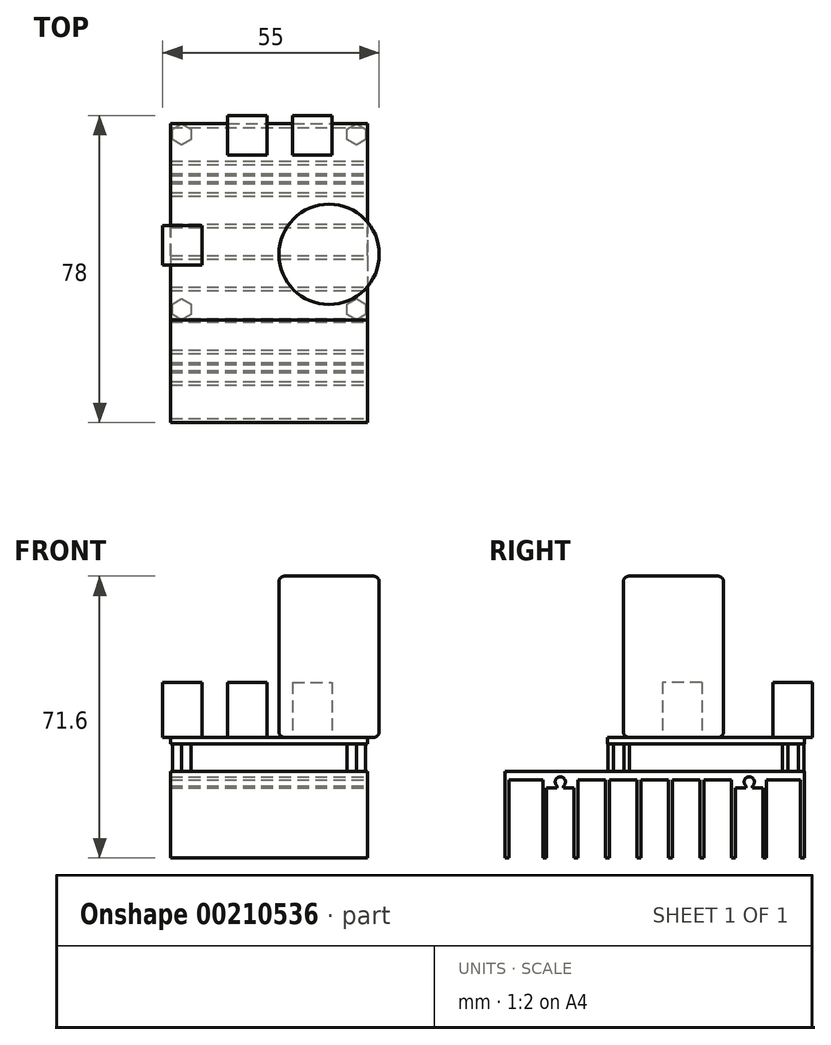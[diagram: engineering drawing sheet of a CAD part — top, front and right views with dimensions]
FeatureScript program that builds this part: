
annotation { "Feature Type Name" : "Feature", "Feature Type Description" : "" }
export const myFeature = defineFeature(function(context is Context, id is Id, definition is map)
    precondition{}
    {
        {
            var Q0;
            Q0=qCreatedBy(makeId("Top.planeOp"),FACE);
            var sketch = newSketch(context, id + "F0", { "sketchPlane" : qUnion([Q0])});
            skLineSegment(sketch, "E0.bottom", {"start": v(-25, 38) * mm, "end": v(25, 38) * mm});
            skLineSegment(sketch, "E0.top", {"start": v(-25, -38) * mm, "end": v(25, -38) * mm});
            skLineSegment(sketch, "E0.left", {"start": v(-25, 38) * mm, "end": v(-25, -38) * mm});
            skLineSegment(sketch, "E0.right", {"start": v(25, 38) * mm, "end": v(25, -38) * mm});
            skLineSegment(sketch, "E1", {"start": v(-25, 38) * mm, "end": v(25, -38) * mm, "construction": true});
            skSolve(sketch);
        }
        {
            var Q0;
            Q0=makeQuery(id+"F0.imprint","IMPRINT",FACE,{"disambiguationData":[TD([[makeQuery(id+"F0.imprint","IMPRINT",EDGE,{"derivedFrom":sQuery(id+"F0.wireOp",EDGE,"E0.bottom")}),-1.0]])]});
            extrude(context, id + "F1", {"entities" : qUnion([Q0]), "oppositeDirection" : true, "depth" : 22 * mm});
        }
        {
            var Q0;
            Q0=qCreatedBy(makeId("Right.planeOp"),FACE);
            var sketch = newSketch(context, id + "F2", { "sketchPlane" : qUnion([Q0])});
            skLineSegment(sketch, "E2.bottom", {"start": v(-37, -2.2) * mm, "end": v(-28.4, -2.2) * mm});
            skLineSegment(sketch, "E2.top", {"start": v(-37, -22) * mm, "end": v(-28.4, -22) * mm});
            skLineSegment(sketch, "E2.left", {"start": v(-37, -2.2) * mm, "end": v(-37, -22) * mm});
            skLineSegment(sketch, "E2.right", {"start": v(-28.4, -2.2) * mm, "end": v(-28.4, -22) * mm});
            skLineSegment(sketch, "E3", {"start": v(0, 0) * mm, "end": v(0, -2.2) * mm, "construction": true});
            skLineSegment(sketch, "E4.bottom", {"start": v(-3.5, -22) * mm, "end": v(3.5, -22) * mm});
            skLineSegment(sketch, "E4.top", {"start": v(-3.5, -2.2) * mm, "end": v(3.5, -2.2) * mm});
            skLineSegment(sketch, "E4.left", {"start": v(-3.5, -22) * mm, "end": v(-3.5, -2.2) * mm});
            skLineSegment(sketch, "E4.right", {"start": v(3.5, -22) * mm, "end": v(3.5, -2.2) * mm});
            skLineSegment(sketch, "E5.1.0.0", {"start": v(-11.5, -22) * mm, "end": v(-11.5, -2.2) * mm});
            skLineSegment(sketch, "E5.1.0.1", {"start": v(-11.5, -2.2) * mm, "end": v(-4.5, -2.2) * mm});
            skLineSegment(sketch, "E5.1.0.2", {"start": v(-4.5, -22) * mm, "end": v(-4.5, -2.2) * mm});
            skLineSegment(sketch, "E5.1.0.3", {"start": v(-11.5, -22) * mm, "end": v(-4.5, -22) * mm});
            skLineSegment(sketch, "E5.2.0.0", {"start": v(-19.5, -22) * mm, "end": v(-19.5, -2.2) * mm});
            skLineSegment(sketch, "E5.2.0.1", {"start": v(-19.5, -2.2) * mm, "end": v(-12.5, -2.2) * mm});
            skLineSegment(sketch, "E5.2.0.2", {"start": v(-12.5, -22) * mm, "end": v(-12.5, -2.2) * mm});
            skLineSegment(sketch, "E5.2.0.3", {"start": v(-19.5, -22) * mm, "end": v(-12.5, -22) * mm});
            skLineSegment(sketch, "E5.3.0.0", {"start": v(-27.5, -22) * mm, "end": v(-27.5, -4.2) * mm});
            skLineSegment(sketch, "E5.3.0.2", {"start": v(-20.5, -22) * mm, "end": v(-20.5, -4.2) * mm});
            skLineSegment(sketch, "E5.3.0.3", {"start": v(-27.5, -22) * mm, "end": v(-20.5, -22) * mm});
            skLineSegment(sketch, "E5.direction1", {"start": v(-3.5, -22) * mm, "end": v(-11.5, -22) * mm, "construction": true});
            skArc(sketch, "E6", {"start": v(-23.2, -3.72) * mm, "mid": v(-24, -1.4) * mm, "end": v(-24.8, -3.72) * mm});
            skPoint(sketch, "E6.centerSnap0", {"position": v(-24, -2.2) * mm});
            skLineSegment(sketch, "E7", {"start": v(-24, -2.7) * mm, "end": v(-24, -1.4) * mm, "construction": true});
            skLineSegment(sketch, "E8", {"start": v(-27.5, -4.2) * mm, "end": v(-24.8, -4.2) * mm});
            skLineSegment(sketch, "E9", {"start": v(-24.8, -3.72) * mm, "end": v(-24.8, -4.2) * mm});
            skLineSegment(sketch, "E10", {"start": v(-23.2, -3.72) * mm, "end": v(-23.2, -4.2) * mm});
            skLineSegment(sketch, "E11.trimOffspring", {"start": v(-23.2, -4.2) * mm, "end": v(-20.5, -4.2) * mm});
            skPoint(sketch, "E12.orphan", {"position": v(-20.5, -2.2) * mm});
            skPoint(sketch, "E13.orphan", {"position": v(-27.5, -2.2) * mm});
            skLineSegment(sketch, "E14.MirrorCS", {"start": v(37, -22) * mm, "end": v(28.4, -22) * mm});
            skLineSegment(sketch, "E15.MirrorCS", {"start": v(28.4, -2.2) * mm, "end": v(28.4, -22) * mm});
            skLineSegment(sketch, "E16.MirrorCS", {"start": v(37, -2.2) * mm, "end": v(37, -22) * mm});
            skLineSegment(sketch, "E17.MirrorCS", {"start": v(37, -2.2) * mm, "end": v(28.4, -2.2) * mm});
            skLineSegment(sketch, "E18.MirrorCS", {"start": v(27.5, -22) * mm, "end": v(27.5, -4.2) * mm});
            skLineSegment(sketch, "E19.MirrorCS", {"start": v(27.5, -4.2) * mm, "end": v(24.8, -4.2) * mm});
            skLineSegment(sketch, "E20.MirrorCS", {"start": v(24.8, -3.72) * mm, "end": v(24.8, -4.2) * mm});
            skArc(sketch, "E21.MirrorCS", {"start": v(23.2, -3.72) * mm, "mid": v(24, -1.4) * mm, "end": v(24.8, -3.72) * mm});
            skLineSegment(sketch, "E22.MirrorCS", {"start": v(23.2, -3.72) * mm, "end": v(23.2, -4.2) * mm});
            skLineSegment(sketch, "E23.MirrorCS", {"start": v(23.2, -4.2) * mm, "end": v(20.5, -4.2) * mm});
            skLineSegment(sketch, "E24.MirrorCS", {"start": v(20.5, -22) * mm, "end": v(20.5, -4.2) * mm});
            skLineSegment(sketch, "E25.MirrorCS", {"start": v(27.5, -22) * mm, "end": v(20.5, -22) * mm});
            skLineSegment(sketch, "E26.MirrorCS", {"start": v(19.5, -22) * mm, "end": v(12.5, -22) * mm});
            skLineSegment(sketch, "E27.MirrorCS", {"start": v(19.5, -22) * mm, "end": v(19.5, -2.2) * mm});
            skLineSegment(sketch, "E28.MirrorCS", {"start": v(19.5, -2.2) * mm, "end": v(12.5, -2.2) * mm});
            skLineSegment(sketch, "E29.MirrorCS", {"start": v(12.5, -22) * mm, "end": v(12.5, -2.2) * mm});
            skLineSegment(sketch, "E30.MirrorCS", {"start": v(11.5, -22) * mm, "end": v(11.5, -2.2) * mm});
            skLineSegment(sketch, "E31.MirrorCS", {"start": v(11.5, -2.2) * mm, "end": v(4.5, -2.2) * mm});
            skLineSegment(sketch, "E32.MirrorCS", {"start": v(4.5, -22) * mm, "end": v(4.5, -2.2) * mm});
            skLineSegment(sketch, "E33.MirrorCS", {"start": v(11.5, -22) * mm, "end": v(4.5, -22) * mm});
            skSolve(sketch);
        }
        {
            var Q0;
            Q0 = qSketchRegion(id + "F2", true);
            extrude(context, id + "F3", {"entities" : qUnion([Q0]), "operationType" : NewBodyOperationType.REMOVE, "endBound" : BoundingType.SYMMETRIC, "oppositeDirection" : true, "depth" : 55 * mm});
        }
        {
            var Q0;
            Q0=makeQuery(id+"F1.opExtrude","CAP_FACE",FACE,{"disambiguationData":[OSD([sQuery(id+"F0.wireOp",EDGE,"E0.bottom"),sQuery(id+"F0.wireOp",EDGE,"E0.top"),sQuery(id+"F0.wireOp",EDGE,"E0.left"),sQuery(id+"F0.wireOp",EDGE,"E0.right")])],"isStart":true});
            var sketch = newSketch(context, id + "F4", { "sketchPlane" : qUnion([Q0])});
            skLineSegment(sketch, "E34.bottom", {"start": v(-22.2, 35.2) * mm, "end": v(22.2, 35.2) * mm, "construction": true});
            skLineSegment(sketch, "E34.top", {"start": v(-22.2, -9.2) * mm, "end": v(22.2, -9.2) * mm, "construction": true});
            skLineSegment(sketch, "E34.left", {"start": v(-22.2, 35.2) * mm, "end": v(-22.2, -9.2) * mm, "construction": true});
            skLineSegment(sketch, "E34.right", {"start": v(22.2, 35.2) * mm, "end": v(22.2, -9.2) * mm, "construction": true});
            skLineSegment(sketch, "E35", {"start": v(-22.2, 35.2) * mm, "end": v(22.2, -9.2) * mm, "construction": true});
            skLineSegment(sketch, "E36", {"start": v(0, 38) * mm, "end": v(0, 13) * mm, "construction": true});
            skPoint(sketch, "E36.startSnap0", {"position": v(0, 13) * mm});
            skCircle(sketch, "E37", {"center": v(-22.2, 35.2) * mm, "radius": 2.71 * mm, "construction": true});
            skLineSegment(sketch, "E38", {"start": v(-22.2, 32.49) * mm, "end": v(-24.55, 33.84) * mm});
            skLineSegment(sketch, "E39", {"start": v(-24.55, 33.84) * mm, "end": v(-24.55, 36.56) * mm});
            skLineSegment(sketch, "E40", {"start": v(-24.55, 36.56) * mm, "end": v(-22.2, 37.91) * mm});
            skLineSegment(sketch, "E41", {"start": v(-22.2, 37.91) * mm, "end": v(-19.85, 36.56) * mm});
            skLineSegment(sketch, "E42", {"start": v(-19.85, 36.56) * mm, "end": v(-19.85, 33.84) * mm});
            skLineSegment(sketch, "E43", {"start": v(-19.85, 33.84) * mm, "end": v(-22.2, 32.49) * mm});
            skLineSegment(sketch, "E44.0.1.0", {"start": v(-22.2, -6.49) * mm, "end": v(-19.85, -7.84) * mm});
            skLineSegment(sketch, "E44.0.1.1", {"start": v(-24.55, -7.84) * mm, "end": v(-22.2, -6.49) * mm});
            skLineSegment(sketch, "E44.0.1.2", {"start": v(-24.55, -10.56) * mm, "end": v(-24.55, -7.84) * mm});
            skLineSegment(sketch, "E44.0.1.3", {"start": v(-22.2, -11.91) * mm, "end": v(-24.55, -10.56) * mm});
            skLineSegment(sketch, "E44.0.1.4", {"start": v(-19.85, -10.56) * mm, "end": v(-22.2, -11.91) * mm});
            skLineSegment(sketch, "E44.0.1.5", {"start": v(-19.85, -7.84) * mm, "end": v(-19.85, -10.56) * mm});
            skLineSegment(sketch, "E44.1.0.0", {"start": v(22.2, 37.91) * mm, "end": v(24.55, 36.56) * mm});
            skLineSegment(sketch, "E44.1.0.1", {"start": v(19.85, 36.56) * mm, "end": v(22.2, 37.91) * mm});
            skLineSegment(sketch, "E44.1.0.2", {"start": v(19.85, 33.84) * mm, "end": v(19.85, 36.56) * mm});
            skLineSegment(sketch, "E44.1.0.3", {"start": v(22.2, 32.49) * mm, "end": v(19.85, 33.84) * mm});
            skLineSegment(sketch, "E44.1.0.4", {"start": v(24.55, 33.84) * mm, "end": v(22.2, 32.49) * mm});
            skLineSegment(sketch, "E44.1.0.5", {"start": v(24.55, 36.56) * mm, "end": v(24.55, 33.84) * mm});
            skLineSegment(sketch, "E44.1.1.0", {"start": v(22.2, -6.49) * mm, "end": v(24.55, -7.84) * mm});
            skLineSegment(sketch, "E44.1.1.1", {"start": v(19.85, -7.84) * mm, "end": v(22.2, -6.49) * mm});
            skLineSegment(sketch, "E44.1.1.2", {"start": v(19.85, -10.56) * mm, "end": v(19.85, -7.84) * mm});
            skLineSegment(sketch, "E44.1.1.3", {"start": v(22.2, -11.91) * mm, "end": v(19.85, -10.56) * mm});
            skLineSegment(sketch, "E44.1.1.4", {"start": v(24.55, -10.56) * mm, "end": v(22.2, -11.91) * mm});
            skLineSegment(sketch, "E44.1.1.5", {"start": v(24.55, -7.84) * mm, "end": v(24.55, -10.56) * mm});
            skLineSegment(sketch, "E44.direction1", {"start": v(-22.2, 37.91) * mm, "end": v(22.2, 37.91) * mm, "construction": true});
            skLineSegment(sketch, "E44.direction2", {"start": v(-22.2, 37.91) * mm, "end": v(-22.2, -6.49) * mm, "construction": true});
            skSolve(sketch);
        }
        {
            var Q0;
            Q0 = qSketchRegion(id + "F4", true);
            extrude(context, id + "F5", {"entities" : qUnion([Q0]), "depth" : 7 * mm});
        }
        {
            var Q0;
            Q0=makeQuery(id+"F5.opExtrude","CAP_FACE",FACE,{"disambiguationData":[OSD([sQuery(id+"F4.wireOp",EDGE,"E38"),sQuery(id+"F4.wireOp",EDGE,"E39"),sQuery(id+"F4.wireOp",EDGE,"E40"),sQuery(id+"F4.wireOp",EDGE,"E41"),sQuery(id+"F4.wireOp",EDGE,"E42"),sQuery(id+"F4.wireOp",EDGE,"E43")])],"isStart":false});
            var sketch = newSketch(context, id + "F6", { "sketchPlane" : qUnion([Q0])});
            skLineSegment(sketch, "E45.bottom", {"start": v(-25, 38) * mm, "end": v(25, 38) * mm});
            skLineSegment(sketch, "E45.top", {"start": v(-25, -12) * mm, "end": v(25, -12) * mm});
            skLineSegment(sketch, "E45.left", {"start": v(-25, 38) * mm, "end": v(-25, -12) * mm});
            skLineSegment(sketch, "E45.right", {"start": v(25, 38) * mm, "end": v(25, -12) * mm});
            skSolve(sketch);
        }
        {
            var Q0;
            Q0=makeQuery(id+"F6.imprint","IMPRINT",FACE,{"disambiguationData":[TD([[makeQuery(id+"F6.imprint","IMPRINT",EDGE,{"derivedFrom":sQuery(id+"F6.wireOp",EDGE,"E45.bottom")}),-1.0]])]});
            var Q1;
            Q1=makeQuery(id+"F6.imprint","IMPRINT",FACE,{"disambiguationData":[TD([[makeQuery(id+"F6.imprint","IMPRINT",EDGE,{"derivedFrom":makeQuery(id+"F5.opExtrude","CAP_EDGE",EDGE,{"disambiguationData":[OSD([sQuery(id+"F4.wireOp",EDGE,"E38")])],"isStart":false})}),-1.0]])]});
            extrude(context, id + "F7", {"entities" : qUnion([Q0, Q1]), "depth" : 1.6 * mm});
        }
        {
            var Q0;
            Q0=makeQuery(id+"F7.opExtrude","CAP_FACE",FACE,{"disambiguationData":[OSD([sQuery(id+"F6.wireOp",EDGE,"E45.bottom"),sQuery(id+"F6.wireOp",EDGE,"E45.top"),sQuery(id+"F6.wireOp",EDGE,"E45.left"),sQuery(id+"F6.wireOp",EDGE,"E45.right")])],"isStart":false});
            var sketch = newSketch(context, id + "F8", { "sketchPlane" : qUnion([Q0])});
            skCircle(sketch, "E46", {"center": v(15.25, 4.75) * mm, "radius": 12.75 * mm});
            skLineSegment(sketch, "E47", {"start": v(15.25, 17.5) * mm, "end": v(15.25, 4.75) * mm, "construction": true});
            skLineSegment(sketch, "E48", {"start": v(15.25, 4.75) * mm, "end": v(28, 4.75) * mm, "construction": true});
            skLineSegment(sketch, "E49", {"start": v(15.25, 4.75) * mm, "end": v(15.25, -8) * mm, "construction": true});
            skSolve(sketch);
        }
        {
            var Q0;
            Q0 = qSketchRegion(id + "F8", true);
            extrude(context, id + "F9", {"entities" : qUnion([Q0]), "depth" : 41 * mm});
        }
        {
            var Q0;
            Q0=makeQuery(id+"F9.opExtrude","CAP_EDGE",EDGE,{"disambiguationData":[OSD([sQuery(id+"F8.wireOp",EDGE,"E46")])],"isStart":false});
            var Q1;
            Q1=makeQuery(id+"F9.opExtrude","CAP_EDGE",EDGE,{"disambiguationData":[OSD([sQuery(id+"F8.wireOp",EDGE,"E46")])],"isStart":true});
            fillet(context, id + "F10", {"entities" : qUnion([Q0, Q1]), "radius" : 1.5 * mm, "tangentPropagation" : true, "allowEdgeOverflow" : false});
        }
        {
            var Q0;
            Q0=makeQuery(id+"F7.opExtrude","CAP_FACE",FACE,{"disambiguationData":[OSD([sQuery(id+"F6.wireOp",EDGE,"E45.bottom"),sQuery(id+"F6.wireOp",EDGE,"E45.top"),sQuery(id+"F6.wireOp",EDGE,"E45.left"),sQuery(id+"F6.wireOp",EDGE,"E45.right")])],"isStart":false});
            var sketch = newSketch(context, id + "F11", { "sketchPlane" : qUnion([Q0])});
            skLineSegment(sketch, "E50.bottom", {"start": v(6, 40) * mm, "end": v(16, 40) * mm});
            skLineSegment(sketch, "E50.top", {"start": v(6, 30) * mm, "end": v(16, 30) * mm});
            skLineSegment(sketch, "E50.left", {"start": v(6, 40) * mm, "end": v(6, 30) * mm});
            skLineSegment(sketch, "E50.right", {"start": v(16, 40) * mm, "end": v(16, 30) * mm});
            skLineSegment(sketch, "E51.bottom", {"start": v(-10.5, 40) * mm, "end": v(-0.5, 40) * mm});
            skLineSegment(sketch, "E51.top", {"start": v(-10.5, 30) * mm, "end": v(-0.5, 30) * mm});
            skLineSegment(sketch, "E51.left", {"start": v(-10.5, 40) * mm, "end": v(-10.5, 30) * mm});
            skLineSegment(sketch, "E51.right", {"start": v(-0.5, 40) * mm, "end": v(-0.5, 30) * mm});
            skLineSegment(sketch, "E52.bottom", {"start": v(-27, 12) * mm, "end": v(-17, 12) * mm});
            skLineSegment(sketch, "E52.top", {"start": v(-27, 2) * mm, "end": v(-17, 2) * mm});
            skLineSegment(sketch, "E52.left", {"start": v(-27, 12) * mm, "end": v(-27, 2) * mm});
            skLineSegment(sketch, "E52.right", {"start": v(-17, 12) * mm, "end": v(-17, 2) * mm});
            skSolve(sketch);
        }
        {
            var Q0;
            {var subQ0=sQuery(id+"F11.wireOp",EDGE,"E52.right");Q0=makeQuery(id+"F11.imprint","IMPRINT",FACE,{"disambiguationData":[TD([[makeQuery(id+"F11.imprint","IMPRINT",EDGE,{"derivedFrom":subQ0}),-1.0]])]});}
            var Q1;
            {var subQ0=sQuery(id+"F11.wireOp",EDGE,"E52.left");Q1=makeQuery(id+"F11.imprint","IMPRINT",FACE,{"disambiguationData":[TD([[makeQuery(id+"F11.imprint","IMPRINT",EDGE,{"derivedFrom":subQ0}),1.0]])]});}
            var Q2;
            {var subQ0=sQuery(id+"F11.wireOp",EDGE,"E51.top");Q2=makeQuery(id+"F11.imprint","IMPRINT",FACE,{"disambiguationData":[TD([[makeQuery(id+"F11.imprint","IMPRINT",EDGE,{"derivedFrom":subQ0}),1.0]])]});}
            var Q3;
            {var subQ0=sQuery(id+"F11.wireOp",EDGE,"E51.bottom");Q3=makeQuery(id+"F11.imprint","IMPRINT",FACE,{"disambiguationData":[TD([[makeQuery(id+"F11.imprint","IMPRINT",EDGE,{"derivedFrom":subQ0}),-1.0]])]});}
            var Q4;
            {var subQ0=sQuery(id+"F11.wireOp",EDGE,"E50.bottom");Q4=makeQuery(id+"F11.imprint","IMPRINT",FACE,{"disambiguationData":[TD([[makeQuery(id+"F11.imprint","IMPRINT",EDGE,{"derivedFrom":subQ0}),-1.0]])]});}
            var Q5;
            {var subQ0=sQuery(id+"F11.wireOp",EDGE,"E50.top");Q5=makeQuery(id+"F11.imprint","IMPRINT",FACE,{"disambiguationData":[TD([[makeQuery(id+"F11.imprint","IMPRINT",EDGE,{"derivedFrom":subQ0}),1.0]])]});}
            extrude(context, id + "F12", {"entities" : qUnion([Q0, Q1, Q2, Q3, Q4, Q5]), "depth" : 14 * mm});
        }
    });
